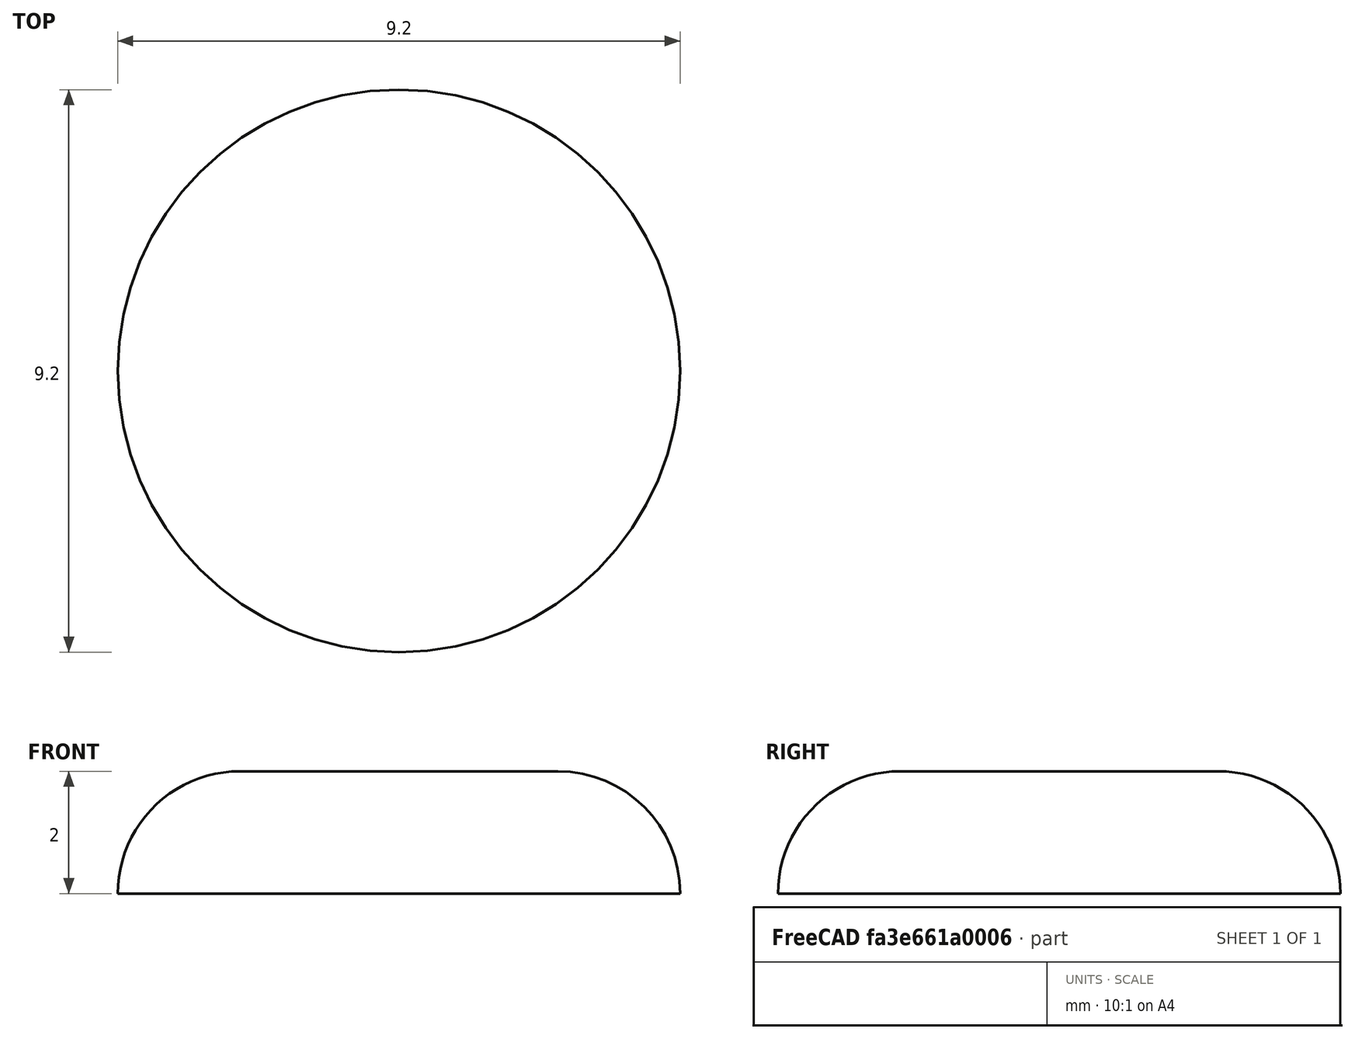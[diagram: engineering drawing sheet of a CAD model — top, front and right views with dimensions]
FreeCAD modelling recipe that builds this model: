
FCSTD DOCUMENT  (FreeCAD 1.1R39024 (Git))
Label: PG03 - bumpon
License: All rights reserved
LicenseURL: https://en.wikipedia.org/wiki/All_rights_reserved
objects: Sketcher::SketchObject×1, PartDesign::Revolution×1, PartDesign::Body×1
note: 6 computed .brp shape members not serialized (recipe doc carries the construction recipe); baked Part::Feature solids carry a one-line shape summary decoded from their .brp

FEATURE [Sketcher::SketchObject] Sketch
  ArcFitTolerance = 1e-06
  AttachmentSupport = -> [XZ_Plane]
  FullyConstrained = true
  MakeInternals = false
  MapMode = 5
  Placement = pos=(0,0,0) rot=(1,0,0;1.5708rad)
  sketch-geometry (4):
    g0: LineSegment StartX=0 StartY=0 StartZ=0 EndX=4.6 EndY=1e-16 EndZ=0
    g1: ArcOfCircle CenterX=2.6 CenterY=1e-16 CenterZ=0 NormalX=0 NormalY=0 NormalZ=1 AngleXU=0 Radius=2 StartAngle=0 EndAngle=1.5708
    g2: LineSegment StartX=2.6 StartY=2 StartZ=0 EndX=0 EndY=2 EndZ=0
    g3: LineSegment StartX=0 StartY=2 StartZ=0 EndX=0 EndY=0 EndZ=0
  constraints (10):
    c: Coincident(g-1,g0)
    c: PointOnObject(g0,g-1)
    c: Perpendicular(g0,g1) = 1.5708
    c: Tangent(g1,g2) = -1.5708
    c: Coincident(g2,g3)
    c: Coincident(g3,g0)
    c: Vertical(g3)
    c: DistanceY(g3,g3) = 2
    c: Radius(g1) = 2
    c: DistanceX(g2,g2) = 2.6
FEATURE [PartDesign::Revolution] Revolution
  Angle = 360
  Angle2 = 60
  Axis = (0,2e-16,1)
  Base = (0,0,0)
  Placement = pos=(0,0,0) rot=(1,0,0;1.5708rad)
  Profile = -> Sketch
  ReferenceAxis = -> Sketch [V_Axis]
  Refine = true
  Reversed = true
  Suppressed = false
  Type = 0
FEATURE [PartDesign::Body] Body
  AllowCompound = true
  Group = -> [Sketch,Revolution]
  Origin = -> Origin
  Tip = -> Revolution
